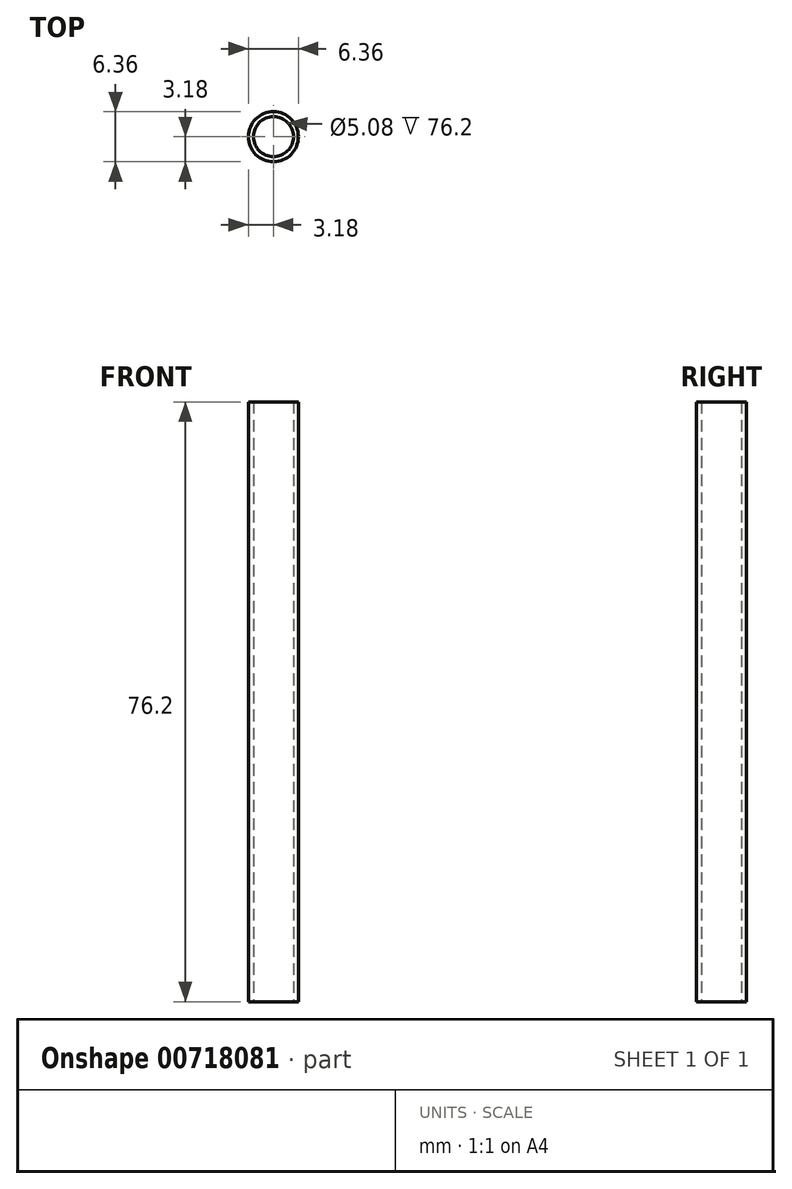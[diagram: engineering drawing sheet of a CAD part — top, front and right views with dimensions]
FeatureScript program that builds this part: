
annotation { "Feature Type Name" : "Feature", "Feature Type Description" : "" }
export const myFeature = defineFeature(function(context is Context, id is Id, definition is map)
    precondition{}
    {
        {
            var Q0;
            Q0=qCreatedBy(makeId("Top.planeOp"),FACE);
            var sketch = newSketch(context, id + "F0", { "sketchPlane" : qUnion([Q0])});
            skCircle(sketch, "E0", {"center": v(0, 0) * mm, "radius": 3.18 * mm});
            skCircle(sketch, "E1", {"center": v(0, 0) * mm, "radius": 2.54 * mm});
            skSolve(sketch);
        }
        {
            var Q0;
            Q0 = qSketchRegion(id + "F0", true);
            extrude(context, id + "F1", {"entities" : qUnion([Q0]), "depth" : 76.2 * mm, "offsetDistance" : 25.4 * mm});
        }
    });
